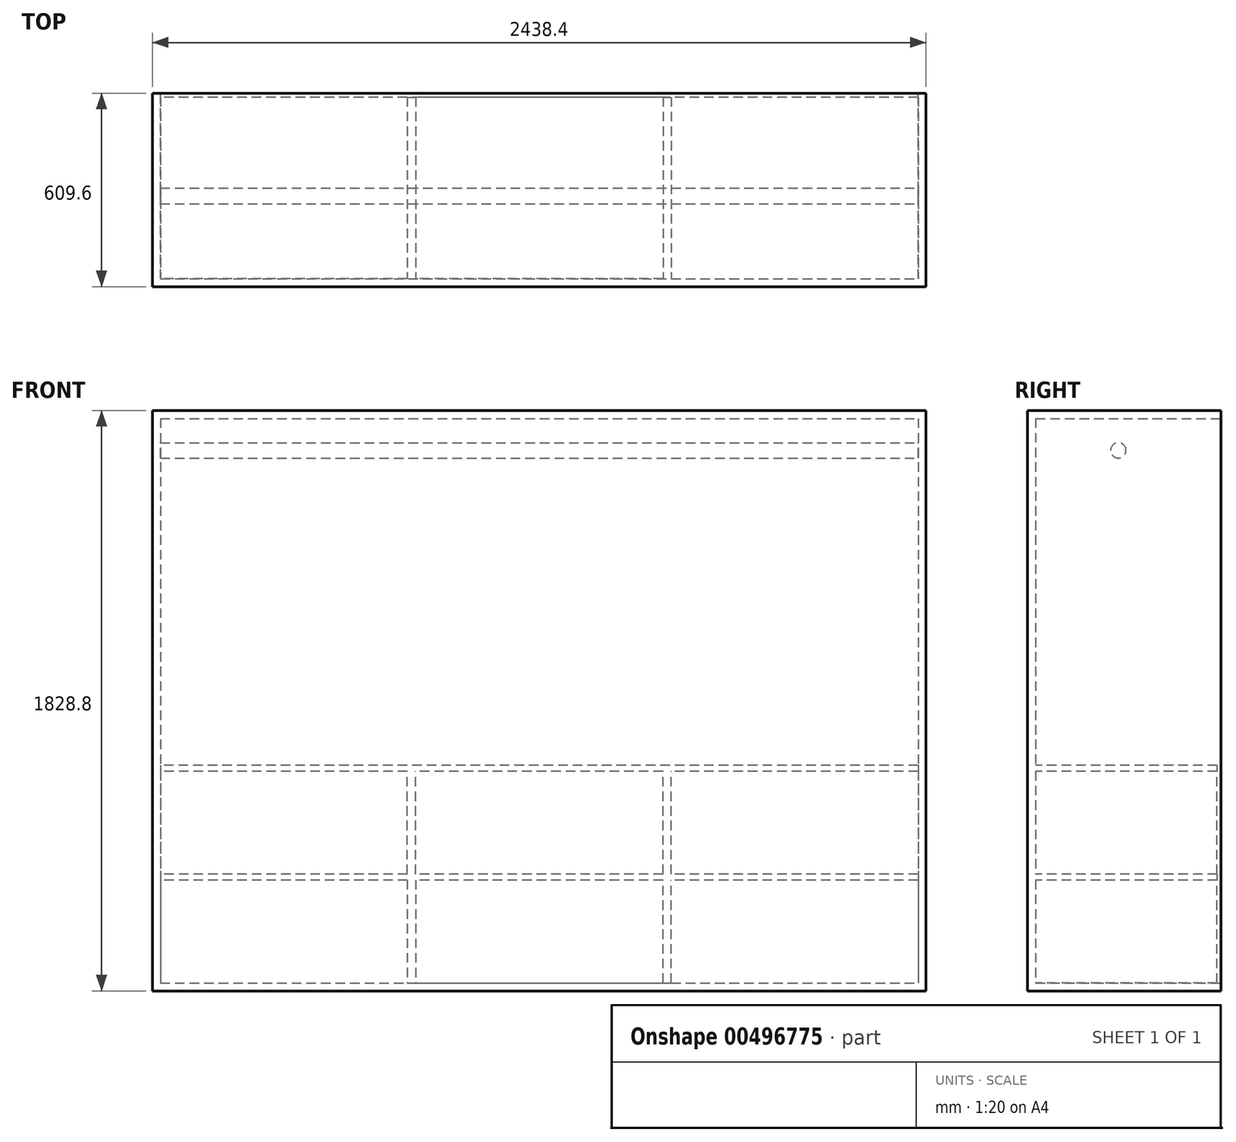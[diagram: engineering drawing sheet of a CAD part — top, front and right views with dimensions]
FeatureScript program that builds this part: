
annotation { "Feature Type Name" : "Feature", "Feature Type Description" : "" }
export const myFeature = defineFeature(function(context is Context, id is Id, definition is map)
    precondition{}
    {
        {
            var Q0;
            Q0=qCreatedBy(makeId("Front.planeOp"),FACE);
            var sketch = newSketch(context, id + "F0", { "sketchPlane" : qUnion([Q0])});
            skLineSegment(sketch, "E0.bottom", {"start": v(-1226.2, 871.16) * mm, "end": v(1212.2, 871.16) * mm});
            skLineSegment(sketch, "E0.top", {"start": v(-1226.2, -957.64) * mm, "end": v(1212.2, -957.64) * mm});
            skLineSegment(sketch, "E0.left", {"start": v(-1226.2, 871.16) * mm, "end": v(-1226.2, -957.64) * mm});
            skLineSegment(sketch, "E0.right", {"start": v(1212.2, 871.16) * mm, "end": v(1212.2, -957.64) * mm});
            skLineSegment(sketch, "E1", {"start": v(-1226.2, -348.04) * mm, "end": v(1212.2, -348.04) * mm});
            skLineSegment(sketch, "E2", {"start": v(1212.2, -348.04) * mm, "end": v(1212.2, -652.84) * mm});
            skLineSegment(sketch, "E3", {"start": v(1212.2, -652.84) * mm, "end": v(-1226.2, -652.84) * mm});
            skSolve(sketch);
        }
        {
            var Q0;
            Q0 = qSketchRegion(id + "F0", true);
            extrude(context, id + "F1", {"entities" : qUnion([Q0]), "depth" : 609.6 * mm});
        }
        {
            var Q0;
            Q0=makeQuery(id+"F1.opExtrude","CAP_FACE",FACE,{"disambiguationData":[OSD([sQuery(id+"F0.wireOp",EDGE,"E0.bottom"),sQuery(id+"F0.wireOp",EDGE,"E0.top"),sQuery(id+"F0.wireOp",EDGE,"E0.left"),sQuery(id+"F0.wireOp",EDGE,"E0.right"),sQuery(id+"F0.wireOp",EDGE,"E2")])],"isStart":true});
            shell(context, id + "F2", {"entities" : qUnion([Q0]), "thickness" : 25.4 * mm});
        }
        {
            var Q0;
            Q0=makeQuery(id+"F2.opShell","OFFSET_FACE",FACE,{"disambiguationData":[OSD([sQuery(id+"F0.wireOp",EDGE,"E0.bottom"),sQuery(id+"F0.wireOp",EDGE,"E0.top"),sQuery(id+"F0.wireOp",EDGE,"E0.left"),sQuery(id+"F0.wireOp",EDGE,"E0.right"),sQuery(id+"F0.wireOp",EDGE,"E2")])]});
            var sketch = newSketch(context, id + "F3", { "sketchPlane" : qUnion([Q0])});
            skLineSegment(sketch, "E4.bottom", {"start": v(-1186.8, -589.34) * mm, "end": v(1200.8, -589.34) * mm});
            skLineSegment(sketch, "E4.top", {"start": v(-1186.8, -608.4) * mm, "end": v(1200.8, -608.4) * mm});
            skLineSegment(sketch, "E4.left", {"start": v(-1186.8, -589.34) * mm, "end": v(-1186.8, -608.4) * mm});
            skLineSegment(sketch, "E4.right", {"start": v(1200.8, -589.34) * mm, "end": v(1200.8, -608.4) * mm});
            skLineSegment(sketch, "E5.bottom", {"start": v(-408.3, -932.24) * mm, "end": v(-382.9, -932.24) * mm});
            skLineSegment(sketch, "E5.top", {"start": v(-408.3, -608.4) * mm, "end": v(-382.9, -608.4) * mm});
            skLineSegment(sketch, "E5.left", {"start": v(-408.3, -932.24) * mm, "end": v(-408.3, -608.4) * mm});
            skLineSegment(sketch, "E5.right", {"start": v(-382.9, -932.24) * mm, "end": v(-382.9, -608.4) * mm});
            skLineSegment(sketch, "E6.bottom", {"start": v(396.88, -608.4) * mm, "end": v(422.28, -608.4) * mm});
            skLineSegment(sketch, "E6.top", {"start": v(396.88, -932.24) * mm, "end": v(422.28, -932.24) * mm});
            skLineSegment(sketch, "E6.left", {"start": v(396.88, -608.4) * mm, "end": v(396.88, -932.24) * mm});
            skLineSegment(sketch, "E6.right", {"start": v(422.28, -608.4) * mm, "end": v(422.28, -932.24) * mm});
            skLineSegment(sketch, "E7.bottom", {"start": v(-408.3, -589.34) * mm, "end": v(-382.9, -589.34) * mm});
            skLineSegment(sketch, "E7.top", {"start": v(-408.3, -265.5) * mm, "end": v(-382.9, -265.5) * mm});
            skLineSegment(sketch, "E7.left", {"start": v(-408.3, -589.34) * mm, "end": v(-408.3, -265.5) * mm});
            skLineSegment(sketch, "E7.right", {"start": v(-382.9, -589.34) * mm, "end": v(-382.9, -265.5) * mm});
            skLineSegment(sketch, "E8.bottom", {"start": v(396.88, -589.34) * mm, "end": v(422.28, -589.34) * mm});
            skLineSegment(sketch, "E8.top", {"start": v(396.88, -265.5) * mm, "end": v(422.28, -265.5) * mm});
            skLineSegment(sketch, "E8.left", {"start": v(396.88, -589.34) * mm, "end": v(396.88, -265.5) * mm});
            skLineSegment(sketch, "E8.right", {"start": v(422.28, -589.34) * mm, "end": v(422.28, -265.5) * mm});
            skLineSegment(sketch, "E9.bottom", {"start": v(-1186.8, -246.44) * mm, "end": v(1200.8, -246.44) * mm});
            skLineSegment(sketch, "E9.top", {"start": v(-1186.8, -265.5) * mm, "end": v(1200.8, -265.5) * mm});
            skLineSegment(sketch, "E9.left", {"start": v(-1186.8, -246.44) * mm, "end": v(-1186.8, -265.5) * mm});
            skLineSegment(sketch, "E9.right", {"start": v(1200.8, -246.44) * mm, "end": v(1200.8, -265.5) * mm});
            skSolve(sketch);
        }
        {
            var Q0;
            Q0 = qSketchRegion(id + "F3", true);
            extrude(context, id + "F4", {"entities" : qUnion([Q0]), "operationType" : NewBodyOperationType.ADD, "depth" : 571.5 * mm});
        }
        {
            var Q0;
            Q0=makeQuery(id+"F1.opExtrude","SWEPT_FACE",FACE,{"disambiguationData":[OSD([sQuery(id+"F0.wireOp",EDGE,"E0.right"),sQuery(id+"F0.wireOp",EDGE,"E2")])]});
            var sketch = newSketch(context, id + "F5", { "sketchPlane" : qUnion([Q0])});
            skCircle(sketch, "E10", {"center": v(-323.94, 745.3) * mm, "radius": 24.26 * mm});
            skSolve(sketch);
        }
        {
            var Q0;
            Q0 = qSketchRegion(id + "F5", true);
            extrude(context, id + "F6", {"entities" : qUnion([Q0]), "operationType" : NewBodyOperationType.ADD, "oppositeDirection" : true, "depth" : 2438.4 * mm});
        }
    });
